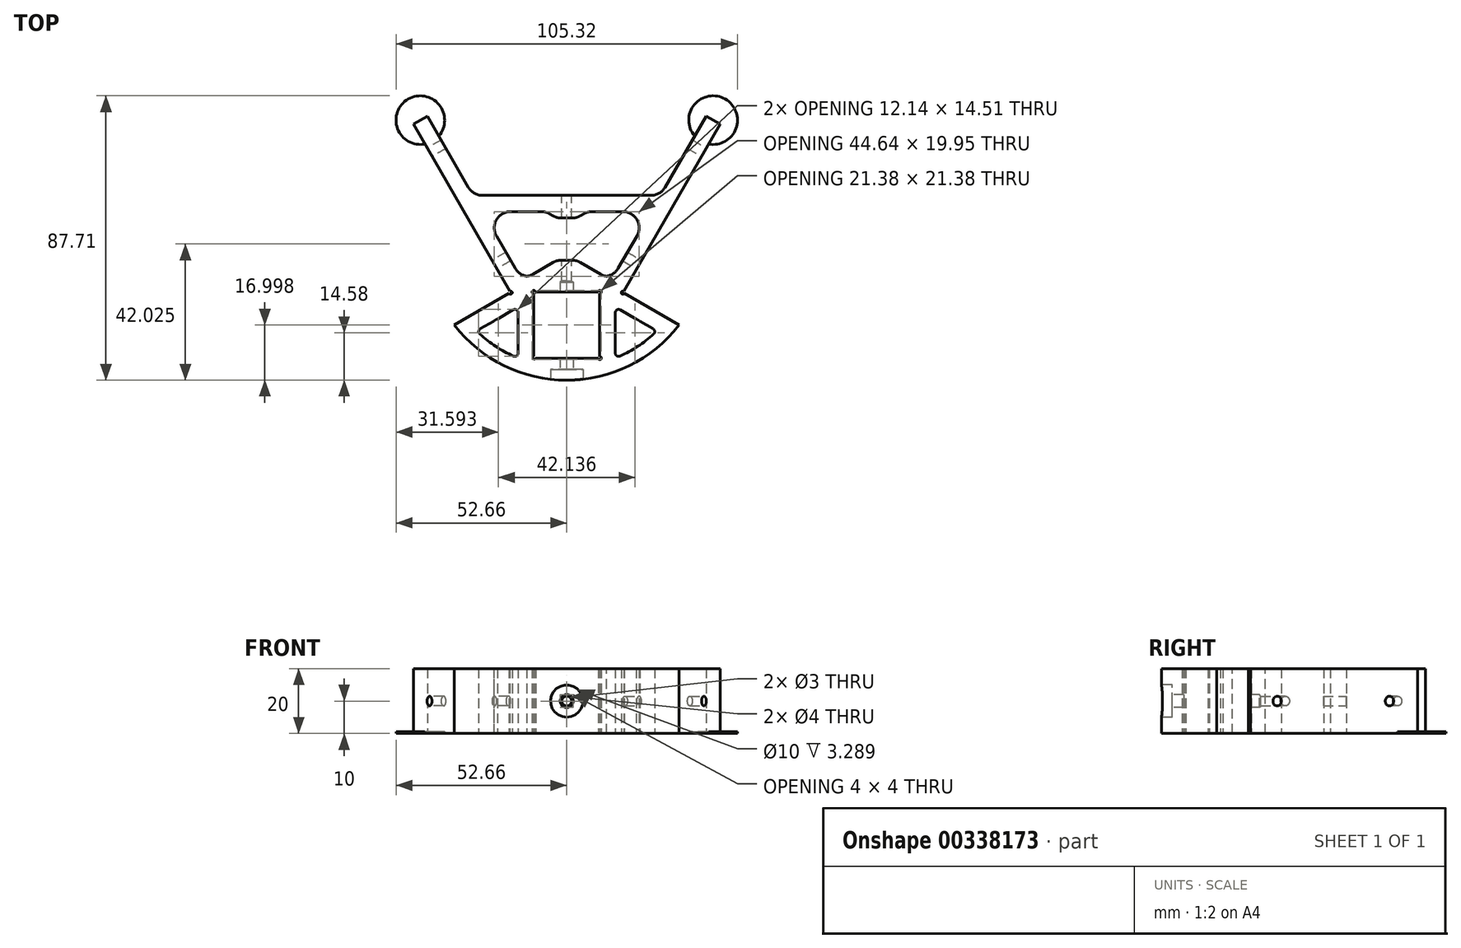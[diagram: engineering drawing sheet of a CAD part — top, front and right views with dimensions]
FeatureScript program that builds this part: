
annotation { "Feature Type Name" : "Feature", "Feature Type Description" : "" }
export const myFeature = defineFeature(function(context is Context, id is Id, definition is map)
    precondition{}
    {
        {
            var Q0;
            Q0=qCreatedBy(makeId("Top.planeOp"),FACE);
            var sketch = newSketch(context, id + "F0", { "sketchPlane" : qUnion([Q0])});
            skLineSegment(sketch, "E0", {"start": v(14.43, 6.05) * mm, "end": v(25.98, 26.05) * mm});
            skLineSegment(sketch, "E1", {"start": v(43, 55.5) * mm, "end": v(47.32, 53) * mm});
            skLineSegment(sketch, "E2", {"start": v(47.32, 53) * mm, "end": v(17.32, 1.05) * mm});
            skLineSegment(sketch, "E3.top", {"start": v(10, 1.05) * mm, "end": v(-10, 1.05) * mm});
            skLineSegment(sketch, "E4", {"start": v(17.32, 1.05) * mm, "end": v(34.64, -8.95) * mm});
            skLineSegment(sketch, "E5", {"start": v(-14.43, 6.05) * mm, "end": v(-25.98, 26.05) * mm});
            skLineSegment(sketch, "E6", {"start": v(-43, 55.5) * mm, "end": v(-47.32, 53) * mm});
            skLineSegment(sketch, "E7", {"start": v(-47.32, 53) * mm, "end": v(-17.32, 1.05) * mm});
            skLineSegment(sketch, "E8", {"start": v(-17.32, 1.05) * mm, "end": v(-34.64, -8.95) * mm});
            skLineSegment(sketch, "E9", {"start": v(-14.43, 6.05) * mm, "end": v(14.43, 6.05) * mm});
            skLineSegment(sketch, "E10", {"start": v(-25.98, 26.05) * mm, "end": v(25.98, 26.05) * mm});
            skLineSegment(sketch, "E11", {"start": v(-28.87, 31.05) * mm, "end": v(28.87, 31.05) * mm});
            skLineSegment(sketch, "E12.trimOffspring", {"start": v(-28.87, 31.05) * mm, "end": v(-43, 55.5) * mm});
            skLineSegment(sketch, "E13.trimOffspring", {"start": v(28.87, 31.05) * mm, "end": v(43, 55.5) * mm});
            skLineSegment(sketch, "E14", {"start": v(27.81, -10.78) * mm, "end": v(15, -3.39) * mm});
            skLineSegment(sketch, "E15", {"start": v(-27.81, -10.78) * mm, "end": v(-15, -3.39) * mm});
            skLineSegment(sketch, "E16", {"start": v(-15, -3.39) * mm, "end": v(-15, -9.7) * mm});
            skLineSegment(sketch, "E17.bottom", {"start": v(-10, 1.05) * mm, "end": v(10, 1.05) * mm});
            skLineSegment(sketch, "E17.top", {"start": v(-10, -18.95) * mm, "end": v(10, -18.95) * mm});
            skLineSegment(sketch, "E17.left", {"start": v(-10, 1.05) * mm, "end": v(-10, -18.95) * mm});
            skLineSegment(sketch, "E17.right", {"start": v(10, 1.05) * mm, "end": v(10, -18.95) * mm});
            skPoint(sketch, "E18.third.point", {"position": v(-4.92, 61.36) * mm});
            skArc(sketch, "E19", {"start": v(15, -19.14) * mm, "mid": v(21.8, -15.58) * mm, "end": v(27.81, -10.78) * mm});
            skLineSegment(sketch, "E20", {"start": v(-15, -9.7) * mm, "end": v(-15, -19.14) * mm});
            skLineSegment(sketch, "E21", {"start": v(15, -3.39) * mm, "end": v(15, -19.14) * mm});
            skArc(sketch, "E22.trimOffspring", {"start": v(-27.81, -10.78) * mm, "mid": v(-21.8, -15.58) * mm, "end": v(-15, -19.14) * mm});
            skArc(sketch, "E23.trimOffspring", {"start": v(-34.64, -8.95) * mm, "mid": v(0, -25.95) * mm, "end": v(34.64, -8.95) * mm});
            skLineSegment(sketch, "E24.0", {"start": v(-10.2, 1.25) * mm, "end": v(10.2, 1.25) * mm});
            skLineSegment(sketch, "E24.1", {"start": v(-10.2, 1.25) * mm, "end": v(-10.2, -19.15) * mm});
            skLineSegment(sketch, "E24.2", {"start": v(-10.2, -19.15) * mm, "end": v(10.2, -19.15) * mm});
            skLineSegment(sketch, "E24.3", {"start": v(10.2, 1.25) * mm, "end": v(10.2, -19.15) * mm});
            skLineSegment(sketch, "E25", {"start": v(-17.98, 26.05) * mm, "end": v(-17.98, 31.05) * mm});
            skLineSegment(sketch, "E26", {"start": v(17.98, 26.05) * mm, "end": v(17.98, 31.05) * mm});
            skLineSegment(sketch, "E27", {"start": v(-28.87, 31.05) * mm, "end": v(-25.98, 26.05) * mm});
            skLineSegment(sketch, "E28", {"start": v(25.98, 26.05) * mm, "end": v(28.87, 31.05) * mm});
            skPoint(sketch, "E29", {"position": v(-19.82, 5.38) * mm});
            skPoint(sketch, "E30", {"position": v(19.82, 5.38) * mm});
            skCircle(sketch, "E31", {"center": v(-19.67, -11.42) * mm, "radius": 4.68 * mm});
            skPoint(sketch, "E31.first.point", {"position": v(-21.8, -15.58) * mm});
            skPoint(sketch, "E31.second.point", {"position": v(-21.4, -7.08) * mm});
            skPoint(sketch, "E31.third.point", {"position": v(-15, -11.64) * mm});
            skCircle(sketch, "E32", {"center": v(19.67, -11.42) * mm, "radius": 4.67 * mm});
            skPoint(sketch, "E32.first.point", {"position": v(21.8, -15.58) * mm});
            skPoint(sketch, "E32.second.point", {"position": v(21.4, -7.08) * mm});
            skPoint(sketch, "E32.third.point", {"position": v(15, -11.42) * mm});
            skArc(sketch, "E33", {"start": v(43.78, 46.89) * mm, "mid": v(48.9, 60.76) * mm, "end": v(39.45, 49.39) * mm});
            skArc(sketch, "E34", {"start": v(-39.45, 49.39) * mm, "mid": v(-48.9, 60.76) * mm, "end": v(-43.78, 46.89) * mm});
            skLineSegment(sketch, "E35", {"start": v(-3, 11.05) * mm, "end": v(3, 11.05) * mm});
            skPoint(sketch, "E36", {"position": v(0, 11.05) * mm});
            skLineSegment(sketch, "E37", {"start": v(-3, 24.05) * mm, "end": v(3, 24.05) * mm});
            skPoint(sketch, "E38", {"position": v(0, 24.05) * mm});
            skLineSegment(sketch, "E39", {"start": v(3, 24.05) * mm, "end": v(6.46, 26.05) * mm});
            skLineSegment(sketch, "E40", {"start": v(-3, 24.05) * mm, "end": v(-6.46, 26.05) * mm});
            skLineSegment(sketch, "E41", {"start": v(-3, 11.05) * mm, "end": v(-11.66, 6.05) * mm});
            skLineSegment(sketch, "E42", {"start": v(3, 11.05) * mm, "end": v(11.66, 6.05) * mm});
            skSolve(sketch);
        }
        {
            var Q0;
            {var subQ4=sQuery(id+"F0.wireOp",EDGE,"E25");Q0=makeQuery(id+"F0.imprint","IMPRINT",FACE,{"disambiguationData":[TD([[makeQuery(id+"F0.imprint","IMPRINT",EDGE,{"derivedFrom":subQ4}),-1.0]])]});}
            var Q1;
            {var subQ2=sQuery(id+"F0.wireOp",EDGE,"E25");Q1=makeQuery(id+"F0.imprint","IMPRINT",FACE,{"disambiguationData":[TD([[makeQuery(id+"F0.imprint","IMPRINT",EDGE,{"derivedFrom":subQ2}),1.0]])]});}
            var Q2;
            {var subQ7=sQuery(id+"F0.wireOp",EDGE,"E0");Q2=makeQuery(id+"F0.imprint","IMPRINT",FACE,{"disambiguationData":[TD([[makeQuery(id+"F0.imprint","IMPRINT",EDGE,{"derivedFrom":subQ7}),-1.0]])]});}
            var Q3;
            Q3=makeQuery(id+"F0.imprint","IMPRINT",FACE,{"disambiguationData":[TD([[makeQuery(id+"F0.imprint","IMPRINT",EDGE,{"derivedFrom":sQuery(id+"F0.wireOp",EDGE,"E35")}),-1.0]])]});
            var Q4;
            Q4=makeQuery(id+"F0.imprint","IMPRINT",FACE,{"disambiguationData":[TD([[makeQuery(id+"F0.imprint","IMPRINT",EDGE,{"derivedFrom":sQuery(id+"F0.wireOp",EDGE,"E37")}),1.0]])]});
            var Q5;
            {var subQ2=sQuery(id+"F0.wireOp",EDGE,"E26");Q5=makeQuery(id+"F0.imprint","IMPRINT",FACE,{"disambiguationData":[TD([[makeQuery(id+"F0.imprint","IMPRINT",EDGE,{"derivedFrom":subQ2}),-1.0]])]});}
            var Q6;
            {var subQ0=sQuery(id+"F0.wireOp",EDGE,"E32");var subQ1=sQuery(id+"F0.wireOp",EDGE,"E19");var subQ2=makeQuery(id+"F0.imprint","INTERSECT",VERTEX,{"disambiguationData":[OD(0.0)],"derivedFrom":[subQ1,subQ0]});Q6=makeQuery(id+"F0.imprint","IMPRINT",FACE,{"disambiguationData":[TD([[makeQuery(id+"F0.imprint","IMPRINT",EDGE,{"disambiguationData":[TD([[subQ2,-1.0]])],"derivedFrom":subQ1}),-1.0]])]});}
            var Q7;
            {var subQ0=sQuery(id+"F0.wireOp",EDGE,"E31");var subQ1=sQuery(id+"F0.wireOp",EDGE,"E22.trimOffspring");var subQ2=makeQuery(id+"F0.imprint","INTERSECT",VERTEX,{"disambiguationData":[OD(0.0)],"derivedFrom":[subQ1,subQ0]});Q7=makeQuery(id+"F0.imprint","IMPRINT",FACE,{"disambiguationData":[TD([[makeQuery(id+"F0.imprint","IMPRINT",EDGE,{"disambiguationData":[TD([[subQ2,-1.0]])],"derivedFrom":subQ1}),-1.0]])]});}
            var Q8;
            {var subQ0=sQuery(id+"F0.wireOp",EDGE,"E31");var subQ1=sQuery(id+"F0.wireOp",EDGE,"E15");var subQ2=makeQuery(id+"F0.imprint","INTERSECT",VERTEX,{"disambiguationData":[OD(0.0)],"derivedFrom":[subQ1,subQ0]});Q8=makeQuery(id+"F0.imprint","IMPRINT",FACE,{"disambiguationData":[TD([[makeQuery(id+"F0.imprint","IMPRINT",EDGE,{"disambiguationData":[TD([[subQ2,-1.0]])],"derivedFrom":subQ1}),1.0]])]});}
            var Q9;
            {var subQ0=sQuery(id+"F0.wireOp",EDGE,"E32");var subQ1=sQuery(id+"F0.wireOp",EDGE,"E14");var subQ2=makeQuery(id+"F0.imprint","INTERSECT",VERTEX,{"disambiguationData":[OD(0.0)],"derivedFrom":[subQ1,subQ0]});Q9=makeQuery(id+"F0.imprint","IMPRINT",FACE,{"disambiguationData":[TD([[makeQuery(id+"F0.imprint","IMPRINT",EDGE,{"disambiguationData":[TD([[subQ2,-1.0]])],"derivedFrom":subQ1}),-1.0]])]});}
            extrude(context, id + "F1", {"entities" : qUnion([Q0, Q1, Q2, Q3, Q4, Q5, Q6, Q7, Q8, Q9]), "depth" : 20 * mm, "offsetDistance" : 25 * mm});
        }
        {
            var Q0;
            Q0=makeQuery(id+"F1.opExtrude","SWEPT_FACE",FACE,{"disambiguationData":[OSD([sQuery(id+"F0.wireOp",EDGE,"E11")])]});
            var sketch = newSketch(context, id + "F2", { "sketchPlane" : qUnion([Q0])});
            skPoint(sketch, "E43", {"position": v(0, 10) * mm});
            skSolve(sketch);
        }
        {
            var Q0;
            Q0=makeQuery(id+"F1.opExtrude","SWEPT_FACE",FACE,{"disambiguationData":[OSD([sQuery(id+"F0.wireOp",EDGE,"E7")])]});
            var sketch = newSketch(context, id + "F3", { "sketchPlane" : qUnion([Q0])});
            skLineSegment(sketch, "E44", {"start": v(-69.57, 10) * mm, "end": v(-9.57, 10) * mm, "construction": true});
            skPoint(sketch, "E45", {"position": v(-59.57, 10) * mm});
            skPoint(sketch, "E46", {"position": v(-19.57, 10) * mm});
            skSolve(sketch);
        }
        {
            var Q0;
            Q0=makeQuery(id+"F1.opExtrude","SWEPT_FACE",FACE,{"disambiguationData":[OSD([sQuery(id+"F0.wireOp",EDGE,"E2")])]});
            var sketch = newSketch(context, id + "F4", { "sketchPlane" : qUnion([Q0])});
            skLineSegment(sketch, "E47", {"start": v(9.57, 10) * mm, "end": v(69.57, 10) * mm, "construction": true});
            skPoint(sketch, "E48", {"position": v(19.57, 10) * mm});
            skPoint(sketch, "E49", {"position": v(59.57, 10) * mm});
            skSolve(sketch);
        }
        {
            var Q0;
            Q0=qCreatedBy(makeId("Front.planeOp"),FACE);
            cPlane(context, id + "F5", {"entities" : qUnion([Q0]), "cplaneType" : CPlaneType.OFFSET, "offset" : 26 * mm, "width" : 150 * mm, "height" : 150 * mm});
        }
        {
            var Q0;
            Q0=qCreatedBy(id+"F5.planeOp",FACE);
            var sketch = newSketch(context, id + "F6", { "sketchPlane" : qUnion([Q0])});
            skPoint(sketch, "E50", {"position": v(0, 10) * mm});
            skSolve(sketch);
        }
        {
            var Q0;
            Q0=sQuery(id+"F4.wireOp",VERTEX,"E48");
            var Q1;
            Q1=sQuery(id+"F4.wireOp",VERTEX,"E49");
            var Q2;
            Q2=makeQuery(id+"F1.opExtrude","SWEPT_BODY",BODY,{"disambiguationData":[OSD([sQuery(id+"F0.wireOp",EDGE,"E0"),sQuery(id+"F0.wireOp",EDGE,"E1"),sQuery(id+"F0.wireOp",EDGE,"E2"),sQuery(id+"F0.wireOp",EDGE,"E4"),sQuery(id+"F0.wireOp",EDGE,"E5"),sQuery(id+"F0.wireOp",EDGE,"E6"),sQuery(id+"F0.wireOp",EDGE,"E7"),sQuery(id+"F0.wireOp",EDGE,"E8"),sQuery(id+"F0.wireOp",EDGE,"E9"),sQuery(id+"F0.wireOp",EDGE,"E10"),sQuery(id+"F0.wireOp",EDGE,"E11"),sQuery(id+"F0.wireOp",EDGE,"E12.trimOffspring"),sQuery(id+"F0.wireOp",EDGE,"E13.trimOffspring"),sQuery(id+"F0.wireOp",EDGE,"E14"),sQuery(id+"F0.wireOp",EDGE,"E15"),sQuery(id+"F0.wireOp",EDGE,"E16"),sQuery(id+"F0.wireOp",EDGE,"E19"),sQuery(id+"F0.wireOp",EDGE,"E20"),sQuery(id+"F0.wireOp",EDGE,"E21"),sQuery(id+"F0.wireOp",EDGE,"E22.trimOffspring"),sQuery(id+"F0.wireOp",EDGE,"E23.trimOffspring"),sQuery(id+"F0.wireOp",EDGE,"E24.0"),sQuery(id+"F0.wireOp",EDGE,"E24.1"),sQuery(id+"F0.wireOp",EDGE,"E24.2"),sQuery(id+"F0.wireOp",EDGE,"E24.3"),sQuery(id+"F0.wireOp",EDGE,"E31"),sQuery(id+"F0.wireOp",EDGE,"E35"),sQuery(id+"F0.wireOp",EDGE,"E37"),sQuery(id+"F0.wireOp",EDGE,"E39"),sQuery(id+"F0.wireOp",EDGE,"E40"),sQuery(id+"F0.wireOp",EDGE,"E41"),sQuery(id+"F0.wireOp",EDGE,"E42")])]});
            hole(context, id + "F7", {"style" : HoleStyle.SIMPLE, "endStyle" : HoleEndStyle.BLIND, "holeDiameter" : 3 * mm, "majorDiameter" : 5 * mm, "holeDepth" : 10 * mm, "isTappedThrough" : true, "tappedDepth" : 12 * mm, "tapClearance" : 3, "locations" : qUnion([Q0, Q1]), "scope" : qUnion([Q2])});
        }
        {
            var Q0;
            Q0=sQuery(id+"F3.wireOp",VERTEX,"E46");
            var Q1;
            Q1=sQuery(id+"F3.wireOp",VERTEX,"E45");
            var Q2;
            Q2=makeQuery(id+"F1.opExtrude","SWEPT_BODY",BODY,{"disambiguationData":[OSD([sQuery(id+"F0.wireOp",EDGE,"E0"),sQuery(id+"F0.wireOp",EDGE,"E1"),sQuery(id+"F0.wireOp",EDGE,"E2"),sQuery(id+"F0.wireOp",EDGE,"E4"),sQuery(id+"F0.wireOp",EDGE,"E5"),sQuery(id+"F0.wireOp",EDGE,"E6"),sQuery(id+"F0.wireOp",EDGE,"E7"),sQuery(id+"F0.wireOp",EDGE,"E8"),sQuery(id+"F0.wireOp",EDGE,"E9"),sQuery(id+"F0.wireOp",EDGE,"E10"),sQuery(id+"F0.wireOp",EDGE,"E11"),sQuery(id+"F0.wireOp",EDGE,"E12.trimOffspring"),sQuery(id+"F0.wireOp",EDGE,"E13.trimOffspring"),sQuery(id+"F0.wireOp",EDGE,"E14"),sQuery(id+"F0.wireOp",EDGE,"E15"),sQuery(id+"F0.wireOp",EDGE,"E16"),sQuery(id+"F0.wireOp",EDGE,"E19"),sQuery(id+"F0.wireOp",EDGE,"E20"),sQuery(id+"F0.wireOp",EDGE,"E21"),sQuery(id+"F0.wireOp",EDGE,"E22.trimOffspring"),sQuery(id+"F0.wireOp",EDGE,"E23.trimOffspring"),sQuery(id+"F0.wireOp",EDGE,"E24.0"),sQuery(id+"F0.wireOp",EDGE,"E24.1"),sQuery(id+"F0.wireOp",EDGE,"E24.2"),sQuery(id+"F0.wireOp",EDGE,"E24.3"),sQuery(id+"F0.wireOp",EDGE,"E31"),sQuery(id+"F0.wireOp",EDGE,"E35"),sQuery(id+"F0.wireOp",EDGE,"E37"),sQuery(id+"F0.wireOp",EDGE,"E39"),sQuery(id+"F0.wireOp",EDGE,"E40"),sQuery(id+"F0.wireOp",EDGE,"E41"),sQuery(id+"F0.wireOp",EDGE,"E42")])]});
            hole(context, id + "F8", {"style" : HoleStyle.SIMPLE, "endStyle" : HoleEndStyle.BLIND, "holeDiameter" : 3 * mm, "majorDiameter" : 5 * mm, "holeDepth" : 10 * mm, "isTappedThrough" : true, "tappedDepth" : 12 * mm, "tapClearance" : 3, "locations" : qUnion([Q0, Q1]), "scope" : qUnion([Q2])});
        }
        {
            var Q0;
            Q0=sQuery(id+"F2.wireOp",VERTEX,"E43");
            var Q1;
            Q1=makeQuery(id+"F1.opExtrude","SWEPT_BODY",BODY,{"disambiguationData":[OSD([sQuery(id+"F0.wireOp",EDGE,"E0"),sQuery(id+"F0.wireOp",EDGE,"E1"),sQuery(id+"F0.wireOp",EDGE,"E2"),sQuery(id+"F0.wireOp",EDGE,"E4"),sQuery(id+"F0.wireOp",EDGE,"E5"),sQuery(id+"F0.wireOp",EDGE,"E6"),sQuery(id+"F0.wireOp",EDGE,"E7"),sQuery(id+"F0.wireOp",EDGE,"E8"),sQuery(id+"F0.wireOp",EDGE,"E9"),sQuery(id+"F0.wireOp",EDGE,"E10"),sQuery(id+"F0.wireOp",EDGE,"E11"),sQuery(id+"F0.wireOp",EDGE,"E12.trimOffspring"),sQuery(id+"F0.wireOp",EDGE,"E13.trimOffspring"),sQuery(id+"F0.wireOp",EDGE,"E14"),sQuery(id+"F0.wireOp",EDGE,"E15"),sQuery(id+"F0.wireOp",EDGE,"E16"),sQuery(id+"F0.wireOp",EDGE,"E19"),sQuery(id+"F0.wireOp",EDGE,"E20"),sQuery(id+"F0.wireOp",EDGE,"E21"),sQuery(id+"F0.wireOp",EDGE,"E22.trimOffspring"),sQuery(id+"F0.wireOp",EDGE,"E23.trimOffspring"),sQuery(id+"F0.wireOp",EDGE,"E24.0"),sQuery(id+"F0.wireOp",EDGE,"E24.1"),sQuery(id+"F0.wireOp",EDGE,"E24.2"),sQuery(id+"F0.wireOp",EDGE,"E24.3"),sQuery(id+"F0.wireOp",EDGE,"E31"),sQuery(id+"F0.wireOp",EDGE,"E35"),sQuery(id+"F0.wireOp",EDGE,"E37"),sQuery(id+"F0.wireOp",EDGE,"E39"),sQuery(id+"F0.wireOp",EDGE,"E40"),sQuery(id+"F0.wireOp",EDGE,"E41"),sQuery(id+"F0.wireOp",EDGE,"E42")])]});
            hole(context, id + "F9", {"style" : HoleStyle.SIMPLE, "endStyle" : HoleEndStyle.BLIND, "holeDiameter" : 3 * mm, "majorDiameter" : 5 * mm, "holeDepth" : 30 * mm, "isTappedThrough" : true, "tappedDepth" : 12 * mm, "tapClearance" : 3, "locations" : qUnion([Q0]), "scope" : qUnion([Q1])});
        }
        {
            var Q0;
            Q0=sQuery(id+"F6.wireOp",VERTEX,"E50");
            var Q1;
            Q1=makeQuery(id+"F1.opExtrude","SWEPT_BODY",BODY,{"disambiguationData":[OSD([sQuery(id+"F0.wireOp",EDGE,"E0"),sQuery(id+"F0.wireOp",EDGE,"E1"),sQuery(id+"F0.wireOp",EDGE,"E2"),sQuery(id+"F0.wireOp",EDGE,"E4"),sQuery(id+"F0.wireOp",EDGE,"E5"),sQuery(id+"F0.wireOp",EDGE,"E6"),sQuery(id+"F0.wireOp",EDGE,"E7"),sQuery(id+"F0.wireOp",EDGE,"E8"),sQuery(id+"F0.wireOp",EDGE,"E9"),sQuery(id+"F0.wireOp",EDGE,"E10"),sQuery(id+"F0.wireOp",EDGE,"E11"),sQuery(id+"F0.wireOp",EDGE,"E12.trimOffspring"),sQuery(id+"F0.wireOp",EDGE,"E13.trimOffspring"),sQuery(id+"F0.wireOp",EDGE,"E14"),sQuery(id+"F0.wireOp",EDGE,"E15"),sQuery(id+"F0.wireOp",EDGE,"E16"),sQuery(id+"F0.wireOp",EDGE,"E19"),sQuery(id+"F0.wireOp",EDGE,"E20"),sQuery(id+"F0.wireOp",EDGE,"E21"),sQuery(id+"F0.wireOp",EDGE,"E22.trimOffspring"),sQuery(id+"F0.wireOp",EDGE,"E23.trimOffspring"),sQuery(id+"F0.wireOp",EDGE,"E24.0"),sQuery(id+"F0.wireOp",EDGE,"E24.1"),sQuery(id+"F0.wireOp",EDGE,"E24.2"),sQuery(id+"F0.wireOp",EDGE,"E24.3"),sQuery(id+"F0.wireOp",EDGE,"E31"),sQuery(id+"F0.wireOp",EDGE,"E35"),sQuery(id+"F0.wireOp",EDGE,"E37"),sQuery(id+"F0.wireOp",EDGE,"E39"),sQuery(id+"F0.wireOp",EDGE,"E40"),sQuery(id+"F0.wireOp",EDGE,"E41"),sQuery(id+"F0.wireOp",EDGE,"E42")])]});
            hole(context, id + "F10", {"style" : HoleStyle.C_BORE, "endStyle" : HoleEndStyle.BLIND, "holeDiameter" : 4 * mm, "cBoreDiameter" : 10 * mm, "cBoreDepth" : 3 * mm, "majorDiameter" : 5 * mm, "holeDepth" : 30 * mm, "isTappedThrough" : true, "tappedDepth" : 12 * mm, "tapClearance" : 3, "locations" : qUnion([Q0]), "scope" : qUnion([Q1])});
        }
        {
            var Q0;
            Q0=sQuery(id+"F0.wireOp",VERTEX,"E24.0.end");
            var Q1;
            Q1=sQuery(id+"F0.wireOp",VERTEX,"E24.2.end");
            var Q2;
            Q2=sQuery(id+"F0.wireOp",VERTEX,"E17.left.end");
            var Q3;
            Q3=sQuery(id+"F0.wireOp",VERTEX,"E24.1.start");
            var Q4;
            Q4=sQuery(id+"F0.wireOp",VERTEX,"E8.start");
            var Q5;
            Q5=sQuery(id+"F0.wireOp",VERTEX,"E4.start");
            var Q6;
            Q6=makeQuery(id+"F1.opExtrude","SWEPT_BODY",BODY,{"disambiguationData":[OSD([sQuery(id+"F0.wireOp",EDGE,"E0"),sQuery(id+"F0.wireOp",EDGE,"E1"),sQuery(id+"F0.wireOp",EDGE,"E2"),sQuery(id+"F0.wireOp",EDGE,"E4"),sQuery(id+"F0.wireOp",EDGE,"E5"),sQuery(id+"F0.wireOp",EDGE,"E6"),sQuery(id+"F0.wireOp",EDGE,"E7"),sQuery(id+"F0.wireOp",EDGE,"E8"),sQuery(id+"F0.wireOp",EDGE,"E9"),sQuery(id+"F0.wireOp",EDGE,"E10"),sQuery(id+"F0.wireOp",EDGE,"E11"),sQuery(id+"F0.wireOp",EDGE,"E12.trimOffspring"),sQuery(id+"F0.wireOp",EDGE,"E13.trimOffspring"),sQuery(id+"F0.wireOp",EDGE,"E14"),sQuery(id+"F0.wireOp",EDGE,"E15"),sQuery(id+"F0.wireOp",EDGE,"E16"),sQuery(id+"F0.wireOp",EDGE,"E19"),sQuery(id+"F0.wireOp",EDGE,"E20"),sQuery(id+"F0.wireOp",EDGE,"E21"),sQuery(id+"F0.wireOp",EDGE,"E22.trimOffspring"),sQuery(id+"F0.wireOp",EDGE,"E23.trimOffspring"),sQuery(id+"F0.wireOp",EDGE,"E24.0"),sQuery(id+"F0.wireOp",EDGE,"E24.1"),sQuery(id+"F0.wireOp",EDGE,"E24.2"),sQuery(id+"F0.wireOp",EDGE,"E24.3"),sQuery(id+"F0.wireOp",EDGE,"E31"),sQuery(id+"F0.wireOp",EDGE,"E35"),sQuery(id+"F0.wireOp",EDGE,"E37"),sQuery(id+"F0.wireOp",EDGE,"E39"),sQuery(id+"F0.wireOp",EDGE,"E40"),sQuery(id+"F0.wireOp",EDGE,"E41"),sQuery(id+"F0.wireOp",EDGE,"E42")])]});
            hole(context, id + "F11", {"style" : HoleStyle.SIMPLE, "endStyle" : HoleEndStyle.BLIND, "oppositeDirection" : true, "holeDiameter" : 1 * mm, "majorDiameter" : 5 * mm, "holeDepth" : 30 * mm, "isTappedThrough" : true, "tappedDepth" : 12 * mm, "tapClearance" : 3, "locations" : qUnion([Q0, Q1, Q2, Q3, Q4, Q5]), "scope" : qUnion([Q6])});
        }
        {
            var Q0;
            Q0=makeQuery(id+"F11.hole-4.boolean.opBoolean","INTERSECT",EDGE,{"derivedFrom":[makeQuery(id+"F1.opExtrude","SWEPT_FACE",FACE,{"disambiguationData":[OSD([sQuery(id+"F0.wireOp",EDGE,"E8")])]}),makeQuery(id+"F11.hole-4.opRevolve","SWEPT_FACE",FACE,{"disambiguationData":[OSD([sQuery(id+"F11.hole-4.sketch.wireOp",EDGE,"core_line_2")])]})]});
            var Q1;
            Q1=makeQuery(id+"F11.hole-4.boolean.opBoolean","INTERSECT",EDGE,{"derivedFrom":[makeQuery(id+"F1.opExtrude","SWEPT_FACE",FACE,{"disambiguationData":[OSD([sQuery(id+"F0.wireOp",EDGE,"E7")])]}),makeQuery(id+"F11.hole-4.opRevolve","SWEPT_FACE",FACE,{"disambiguationData":[OSD([sQuery(id+"F11.hole-4.sketch.wireOp",EDGE,"core_line_2")])]})]});
            var Q2;
            Q2=makeQuery(id+"F11.hole-1.boolean.opBoolean","INTERSECT",EDGE,{"derivedFrom":[makeQuery(id+"F1.opExtrude","SWEPT_FACE",FACE,{"disambiguationData":[OSD([sQuery(id+"F0.wireOp",EDGE,"E24.3")])]}),makeQuery(id+"F11.hole-1.opRevolve","SWEPT_FACE",FACE,{"disambiguationData":[OSD([sQuery(id+"F11.hole-1.sketch.wireOp",EDGE,"core_line_2")])]})]});
            var Q3;
            Q3=makeQuery(id+"F11.hole-1.boolean.opBoolean","INTERSECT",EDGE,{"derivedFrom":[makeQuery(id+"F1.opExtrude","SWEPT_FACE",FACE,{"disambiguationData":[OSD([sQuery(id+"F0.wireOp",EDGE,"E24.2")])]}),makeQuery(id+"F11.hole-1.opRevolve","SWEPT_FACE",FACE,{"disambiguationData":[OSD([sQuery(id+"F11.hole-1.sketch.wireOp",EDGE,"core_line_2")])]})]});
            var Q4;
            Q4=makeQuery(id+"F11.hole-2.boolean.opBoolean","INTERSECT",EDGE,{"derivedFrom":[makeQuery(id+"F1.opExtrude","SWEPT_FACE",FACE,{"disambiguationData":[OSD([sQuery(id+"F0.wireOp",EDGE,"E24.1")])]}),makeQuery(id+"F11.hole-2.opRevolve","SWEPT_FACE",FACE,{"disambiguationData":[OSD([sQuery(id+"F11.hole-2.sketch.wireOp",EDGE,"core_line_2")])]})]});
            var Q5;
            Q5=makeQuery(id+"F11.hole-2.boolean.opBoolean","INTERSECT",EDGE,{"derivedFrom":[makeQuery(id+"F1.opExtrude","SWEPT_FACE",FACE,{"disambiguationData":[OSD([sQuery(id+"F0.wireOp",EDGE,"E24.2")])]}),makeQuery(id+"F11.hole-2.opRevolve","SWEPT_FACE",FACE,{"disambiguationData":[OSD([sQuery(id+"F11.hole-2.sketch.wireOp",EDGE,"core_line_2")])]})]});
            var Q6;
            Q6=makeQuery(id+"F11.hole-5.boolean.opBoolean","INTERSECT",EDGE,{"derivedFrom":[makeQuery(id+"F1.opExtrude","SWEPT_FACE",FACE,{"disambiguationData":[OSD([sQuery(id+"F0.wireOp",EDGE,"E4")])]}),makeQuery(id+"F11.hole-5.opRevolve","SWEPT_FACE",FACE,{"disambiguationData":[OSD([sQuery(id+"F11.hole-5.sketch.wireOp",EDGE,"core_line_2")])]})]});
            var Q7;
            Q7=makeQuery(id+"F11.hole-5.boolean.opBoolean","INTERSECT",EDGE,{"derivedFrom":[makeQuery(id+"F1.opExtrude","SWEPT_FACE",FACE,{"disambiguationData":[OSD([sQuery(id+"F0.wireOp",EDGE,"E2")])]}),makeQuery(id+"F11.hole-5.opRevolve","SWEPT_FACE",FACE,{"disambiguationData":[OSD([sQuery(id+"F11.hole-5.sketch.wireOp",EDGE,"core_line_2")])]})]});
            var Q8;
            Q8=makeQuery(id+"F11.hole-3.boolean.opBoolean","INTERSECT",EDGE,{"derivedFrom":[makeQuery(id+"F1.opExtrude","SWEPT_FACE",FACE,{"disambiguationData":[OSD([sQuery(id+"F0.wireOp",EDGE,"E24.0")])]}),makeQuery(id+"F11.hole-3.opRevolve","SWEPT_FACE",FACE,{"disambiguationData":[OSD([sQuery(id+"F11.hole-3.sketch.wireOp",EDGE,"core_line_2")])]})]});
            var Q9;
            Q9=makeQuery(id+"F11.hole-3.boolean.opBoolean","INTERSECT",EDGE,{"derivedFrom":[makeQuery(id+"F1.opExtrude","SWEPT_FACE",FACE,{"disambiguationData":[OSD([sQuery(id+"F0.wireOp",EDGE,"E24.1")])]}),makeQuery(id+"F11.hole-3.opRevolve","SWEPT_FACE",FACE,{"disambiguationData":[OSD([sQuery(id+"F11.hole-3.sketch.wireOp",EDGE,"core_line_2")])]})]});
            var Q10;
            Q10=makeQuery(id+"F11.hole-0.boolean.opBoolean","INTERSECT",EDGE,{"derivedFrom":[makeQuery(id+"F1.opExtrude","SWEPT_FACE",FACE,{"disambiguationData":[OSD([sQuery(id+"F0.wireOp",EDGE,"E24.0")])]}),makeQuery(id+"F11.hole-0.opRevolve","SWEPT_FACE",FACE,{"disambiguationData":[OSD([sQuery(id+"F11.hole-0.sketch.wireOp",EDGE,"core_line_2")])]})]});
            var Q11;
            Q11=makeQuery(id+"F11.hole-0.boolean.opBoolean","INTERSECT",EDGE,{"derivedFrom":[makeQuery(id+"F1.opExtrude","SWEPT_FACE",FACE,{"disambiguationData":[OSD([sQuery(id+"F0.wireOp",EDGE,"E24.3")])]}),makeQuery(id+"F11.hole-0.opRevolve","SWEPT_FACE",FACE,{"disambiguationData":[OSD([sQuery(id+"F11.hole-0.sketch.wireOp",EDGE,"core_line_2")])]})]});
            var Q12;
            Q12=makeQuery(id+"F1.opExtrude","SWEPT_EDGE",EDGE,{"disambiguationData":[OSD([sQuery(id+"F0.wireOp",EDGE,"E19"),sQuery(id+"F0.wireOp",EDGE,"E21")])]});
            var Q13;
            Q13=makeQuery(id+"F1.opExtrude","SWEPT_EDGE",EDGE,{"disambiguationData":[OSD([sQuery(id+"F0.wireOp",EDGE,"E14"),sQuery(id+"F0.wireOp",EDGE,"E21")])]});
            var Q14;
            Q14=makeQuery(id+"F1.opExtrude","SWEPT_EDGE",EDGE,{"disambiguationData":[OSD([sQuery(id+"F0.wireOp",EDGE,"E14"),sQuery(id+"F0.wireOp",EDGE,"E19")])]});
            var Q15;
            Q15=makeQuery(id+"F1.opExtrude","SWEPT_EDGE",EDGE,{"disambiguationData":[OSD([sQuery(id+"F0.wireOp",EDGE,"E15"),sQuery(id+"F0.wireOp",EDGE,"E16")])]});
            var Q16;
            Q16=makeQuery(id+"F1.opExtrude","SWEPT_EDGE",EDGE,{"disambiguationData":[OSD([sQuery(id+"F0.wireOp",EDGE,"E15"),sQuery(id+"F0.wireOp",EDGE,"E22.trimOffspring")])]});
            var Q17;
            Q17=makeQuery(id+"F1.opExtrude","SWEPT_EDGE",EDGE,{"disambiguationData":[OSD([sQuery(id+"F0.wireOp",EDGE,"E20"),sQuery(id+"F0.wireOp",EDGE,"E22.trimOffspring")])]});
            fillet(context, id + "F12", {"entities" : qUnion([Q0, Q1, Q2, Q3, Q4, Q5, Q6, Q7, Q8, Q9, Q10, Q11, Q12, Q13, Q14, Q15, Q16, Q17]), "radius" : 1 * mm, "tangentPropagation" : true, "allowEdgeOverflow" : false});
        }
        {
            var Q0;
            Q0=makeQuery(id+"F1.opExtrude","SWEPT_EDGE",EDGE,{"disambiguationData":[OSD([sQuery(id+"F0.wireOp",EDGE,"E5"),sQuery(id+"F0.wireOp",EDGE,"E10"),sQuery(id+"F0.wireOp",EDGE,"E27")])]});
            var Q1;
            Q1=makeQuery(id+"F1.opExtrude","SWEPT_EDGE",EDGE,{"disambiguationData":[OSD([sQuery(id+"F0.wireOp",EDGE,"E0"),sQuery(id+"F0.wireOp",EDGE,"E10"),sQuery(id+"F0.wireOp",EDGE,"E28")])]});
            var Q2;
            Q2=makeQuery(id+"F1.opExtrude","SWEPT_EDGE",EDGE,{"disambiguationData":[OSD([sQuery(id+"F0.wireOp",EDGE,"E0"),sQuery(id+"F0.wireOp",EDGE,"E9")])]});
            var Q3;
            Q3=makeQuery(id+"F1.opExtrude","SWEPT_EDGE",EDGE,{"disambiguationData":[OSD([sQuery(id+"F0.wireOp",EDGE,"E5"),sQuery(id+"F0.wireOp",EDGE,"E9")])]});
            var Q4;
            Q4=makeQuery(id+"F1.opExtrude","SWEPT_EDGE",EDGE,{"disambiguationData":[OSD([sQuery(id+"F0.wireOp",EDGE,"E11"),sQuery(id+"F0.wireOp",EDGE,"E12.trimOffspring"),sQuery(id+"F0.wireOp",EDGE,"E27")])]});
            var Q5;
            Q5=makeQuery(id+"F1.opExtrude","SWEPT_EDGE",EDGE,{"disambiguationData":[OSD([sQuery(id+"F0.wireOp",EDGE,"E11"),sQuery(id+"F0.wireOp",EDGE,"E13.trimOffspring"),sQuery(id+"F0.wireOp",EDGE,"E28")])]});
            var Q6;
            Q6=makeQuery(id+"F1.opExtrude","SWEPT_EDGE",EDGE,{"disambiguationData":[OSD([sQuery(id+"F0.wireOp",EDGE,"E10"),sQuery(id+"F0.wireOp",EDGE,"E39")])]});
            var Q7;
            Q7=makeQuery(id+"F1.opExtrude","SWEPT_EDGE",EDGE,{"disambiguationData":[OSD([sQuery(id+"F0.wireOp",EDGE,"E37"),sQuery(id+"F0.wireOp",EDGE,"E39")])]});
            var Q8;
            Q8=makeQuery(id+"F1.opExtrude","SWEPT_EDGE",EDGE,{"disambiguationData":[OSD([sQuery(id+"F0.wireOp",EDGE,"E37"),sQuery(id+"F0.wireOp",EDGE,"E40")])]});
            var Q9;
            Q9=makeQuery(id+"F1.opExtrude","SWEPT_EDGE",EDGE,{"disambiguationData":[OSD([sQuery(id+"F0.wireOp",EDGE,"E10"),sQuery(id+"F0.wireOp",EDGE,"E40")])]});
            var Q10;
            Q10=makeQuery(id+"F1.opExtrude","SWEPT_EDGE",EDGE,{"disambiguationData":[OSD([sQuery(id+"F0.wireOp",EDGE,"E9"),sQuery(id+"F0.wireOp",EDGE,"E41")])]});
            var Q11;
            Q11=makeQuery(id+"F1.opExtrude","SWEPT_EDGE",EDGE,{"disambiguationData":[OSD([sQuery(id+"F0.wireOp",EDGE,"E35"),sQuery(id+"F0.wireOp",EDGE,"E41")])]});
            var Q12;
            Q12=makeQuery(id+"F1.opExtrude","SWEPT_EDGE",EDGE,{"disambiguationData":[OSD([sQuery(id+"F0.wireOp",EDGE,"E35"),sQuery(id+"F0.wireOp",EDGE,"E42")])]});
            var Q13;
            Q13=makeQuery(id+"F1.opExtrude","SWEPT_EDGE",EDGE,{"disambiguationData":[OSD([sQuery(id+"F0.wireOp",EDGE,"E9"),sQuery(id+"F0.wireOp",EDGE,"E42")])]});
            fillet(context, id + "F13", {"entities" : qUnion([Q0, Q1, Q2, Q3, Q4, Q5, Q6, Q7, Q8, Q9, Q10, Q11, Q12, Q13]), "radius" : 5 * mm, "tangentPropagation" : true, "allowEdgeOverflow" : false});
        }
        {
            var Q0;
            {var subQ0=sQuery(id+"F0.wireOp",EDGE,"E6");Q0=makeQuery(id+"F0.imprint","IMPRINT",FACE,{"disambiguationData":[TD([[makeQuery(id+"F0.imprint","IMPRINT",EDGE,{"derivedFrom":subQ0}),-1.0]])]});}
            var Q1;
            {var subQ0=sQuery(id+"F0.wireOp",EDGE,"E1");Q1=makeQuery(id+"F0.imprint","IMPRINT",FACE,{"disambiguationData":[TD([[makeQuery(id+"F0.imprint","IMPRINT",EDGE,{"derivedFrom":subQ0}),1.0]])]});}
            extrude(context, id + "F14", {"entities" : qUnion([Q0, Q1]), "operationType" : NewBodyOperationType.ADD, "depth" : 0.5 * mm, "offsetDistance" : 25 * mm});
        }
    });
